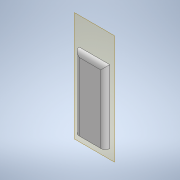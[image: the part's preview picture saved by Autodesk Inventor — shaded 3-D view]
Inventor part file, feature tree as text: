
AUTODESK INVENTOR PART (.ipt)
format: ipt  version: 2021 (Build 250183000, 183)  size: 114,688 bytes
history: native  units: mm
features: other x5, extrude x1, fillet x1, sketch x1, reference x1
ambient origin geometry x8: Origin, YZ Plane, XZ Plane, XY Plane, X Axis, Y Axis, Z Axis, Center Point
bodies: Body1 (feature_tree)
feature tree (9):
  other  "Bryła1"
  other  "Płaszczyzna konstrukcyjna1"
  extrude  "Wyciągnięcie proste1"  Depth=1.0mm
  fillet  "Zaokrąglenie1"  Radius=1.5mm
  sketch  "Szkic1"
  reference  "Odniesienie1"
  parser-record x1  (decoder bookkeeping rows leaked as tree rows — omitted from the tree; the rows remain in map.json)
  other  "model tensometru.iam"
  other  "tensometr:1"
note: 1 file-system path scrubbed to <path> (originals preserved in map.json)
